# Revit family: Outdoor-Kitchen-Cabinets_Kalamazoo_Sink-Based-Cabinets_Arcadia
name_source: partatom
category: Specialty Equipment
revit_build: Autodesk Revit 2018 (Build: 20190510_1515(x64)
units: mm (PartAtom-declared; Revit-internal decimal feet)

## family parameters
Always vertical = Yes
Cut with Voids When Loaded = No
OmniClass Number = 23.40.40.11
OmniClass Title = Specialized Food Storage and Display Furnishings
Part Type = Normal
Room Calculation Point = No
Round Connector Dimension = Use Diameter
Shared = No
Work Plane-Based = No

## types (3) — shared parameters
Assembly Code = E1090300
Depth = 29 1/8"
Keynote = 11400
Manufacturer = Kalamazoo Outdoor Gourmet
Product Material = Kalamazoo - Stainless Steel - 304 OR 316L
Product data url = https://www.bimobject.com
URL = https://kalamazoogourmet.com
Ι_Gnrc Mdl Optn 01 = Extension : +3/4"
Ι_Gnrc Mdl Optn 02 = Extension : -3/4"

## per-type parameters (varying)
| type | Description | Weight (lb) | Width | Ι_Gd Rl100 | Ι_Gd Rl120 |
| KD-24-SNK | Arcadia 24-inch Sink Base Cabinet | 220.00 lbf | 24" | Yes | No |
| KD-30-SNK | Arcadia 30-inch Sink Base Cabinet | 240.00 lbf | 30" | No | Yes |
| KD-36-SNK | Arcadia 36-inch Sink Base Cabinet | 250.00 lbf | 36" | No | Yes |

note: column(s) folded — value = type name in every type: Model

## geometry (parser evidence)
native form markers: Sweep x5
no freeform markers — native parametric forms only
